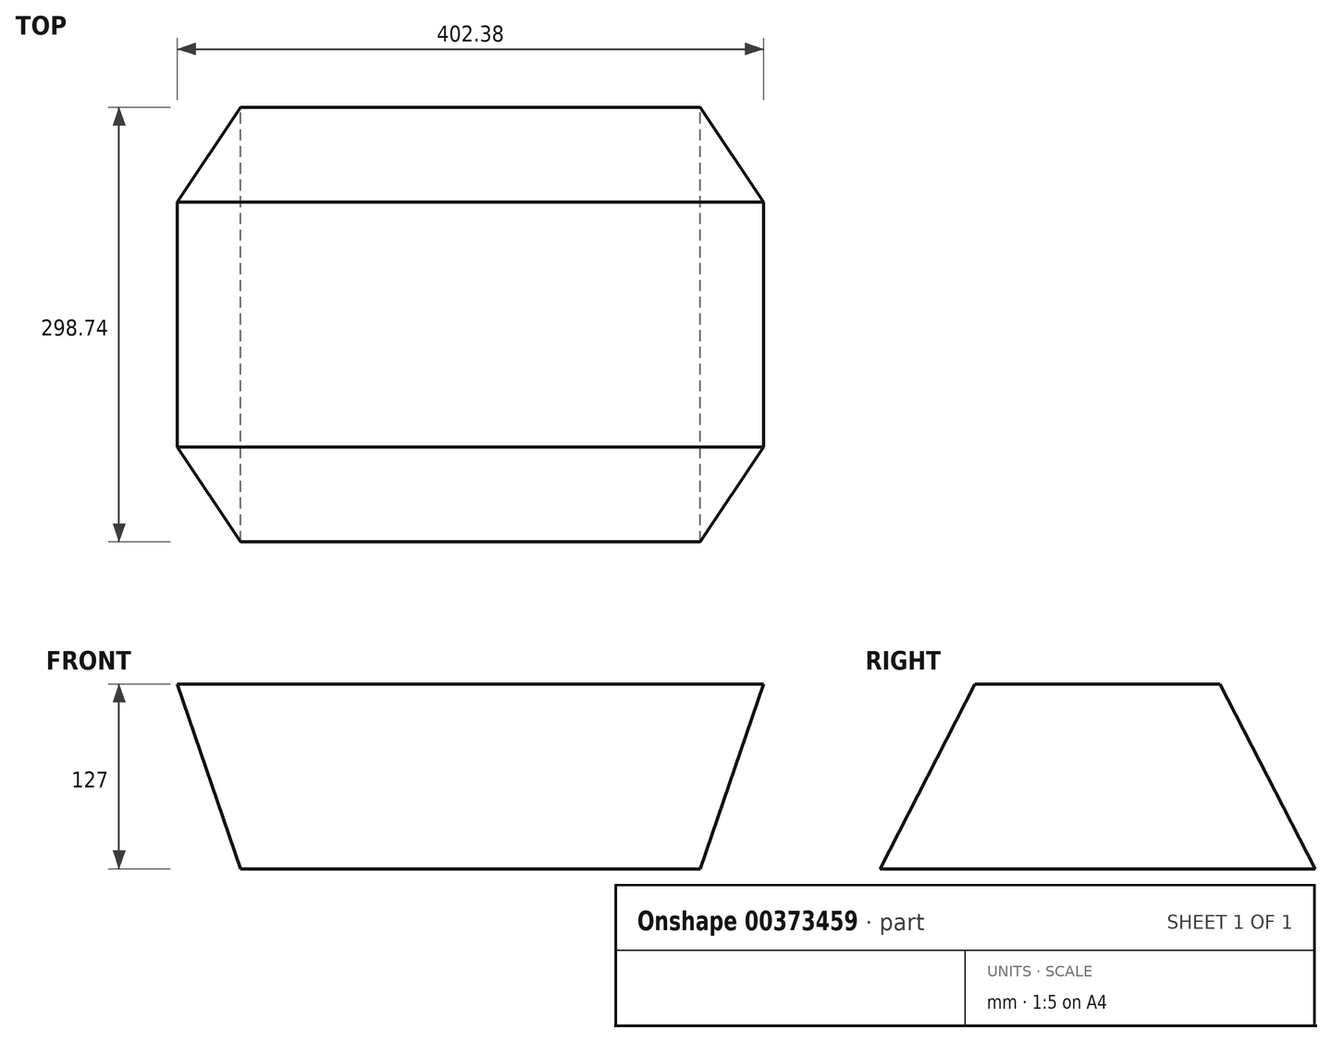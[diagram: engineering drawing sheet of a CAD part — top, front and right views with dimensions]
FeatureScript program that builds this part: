
annotation { "Feature Type Name" : "Feature", "Feature Type Description" : "" }
export const myFeature = defineFeature(function(context is Context, id is Id, definition is map)
    precondition{}
    {
        {
            var Q0;
            Q0=qCreatedBy(makeId("Top.planeOp"),FACE);
            cPlane(context, id + "F0", {"entities" : qUnion([Q0]), "cplaneType" : CPlaneType.OFFSET, "offset" : 127 * mm, "width" : 152.4 * mm, "height" : 152.4 * mm});
        }
        {
            var Q0;
            Q0=qCreatedBy(makeId("Top.planeOp"),FACE);
            var sketch = newSketch(context, id + "F1", { "sketchPlane" : qUnion([Q0])});
            skLineSegment(sketch, "E0.bottom", {"start": v(157.94, -149.37) * mm, "end": v(-157.94, -149.37) * mm});
            skLineSegment(sketch, "E0.top", {"start": v(157.94, 149.37) * mm, "end": v(-157.94, 149.37) * mm});
            skLineSegment(sketch, "E0.left", {"start": v(157.94, -149.37) * mm, "end": v(157.94, 149.37) * mm});
            skLineSegment(sketch, "E0.right", {"start": v(-157.94, -149.37) * mm, "end": v(-157.94, 149.37) * mm});
            skPoint(sketch, "E0.middle", {"position": v(0, 0) * mm});
            skSolve(sketch);
        }
        {
            var Q0;
            Q0=qCreatedBy(id+"F0.planeOp",FACE);
            var sketch = newSketch(context, id + "F2", { "sketchPlane" : qUnion([Q0])});
            skLineSegment(sketch, "E1.bottom", {"start": v(201.19, 84.12) * mm, "end": v(-201.19, 84.12) * mm});
            skLineSegment(sketch, "E1.top", {"start": v(201.19, -84.12) * mm, "end": v(-201.19, -84.12) * mm});
            skLineSegment(sketch, "E1.left", {"start": v(201.19, 84.12) * mm, "end": v(201.19, -84.12) * mm});
            skLineSegment(sketch, "E1.right", {"start": v(-201.19, 84.12) * mm, "end": v(-201.19, -84.12) * mm});
            skPoint(sketch, "E1.middle", {"position": v(0, 0) * mm});
            skSolve(sketch);
        }
        {
            var Q0;
            Q0=makeQuery(id+"F1.imprint","IMPRINT",FACE,{"disambiguationData":[TD([[makeQuery(id+"F1.imprint","IMPRINT",EDGE,{"derivedFrom":sQuery(id+"F1.wireOp",EDGE,"E0.bottom")}),-1.0]])]});
            var Q1;
            Q1=makeQuery(id+"F2.imprint","IMPRINT",FACE,{"disambiguationData":[TD([[makeQuery(id+"F2.imprint","IMPRINT",EDGE,{"derivedFrom":sQuery(id+"F2.wireOp",EDGE,"E1.bottom")}),1.0]])]});
            loft(context, id + "F3", {"sheetProfilesArray" : [{ "sheetProfileEntities" : qUnion([Q0]) }, { "sheetProfileEntities" : qUnion([Q1]) }]});
        }
    });
